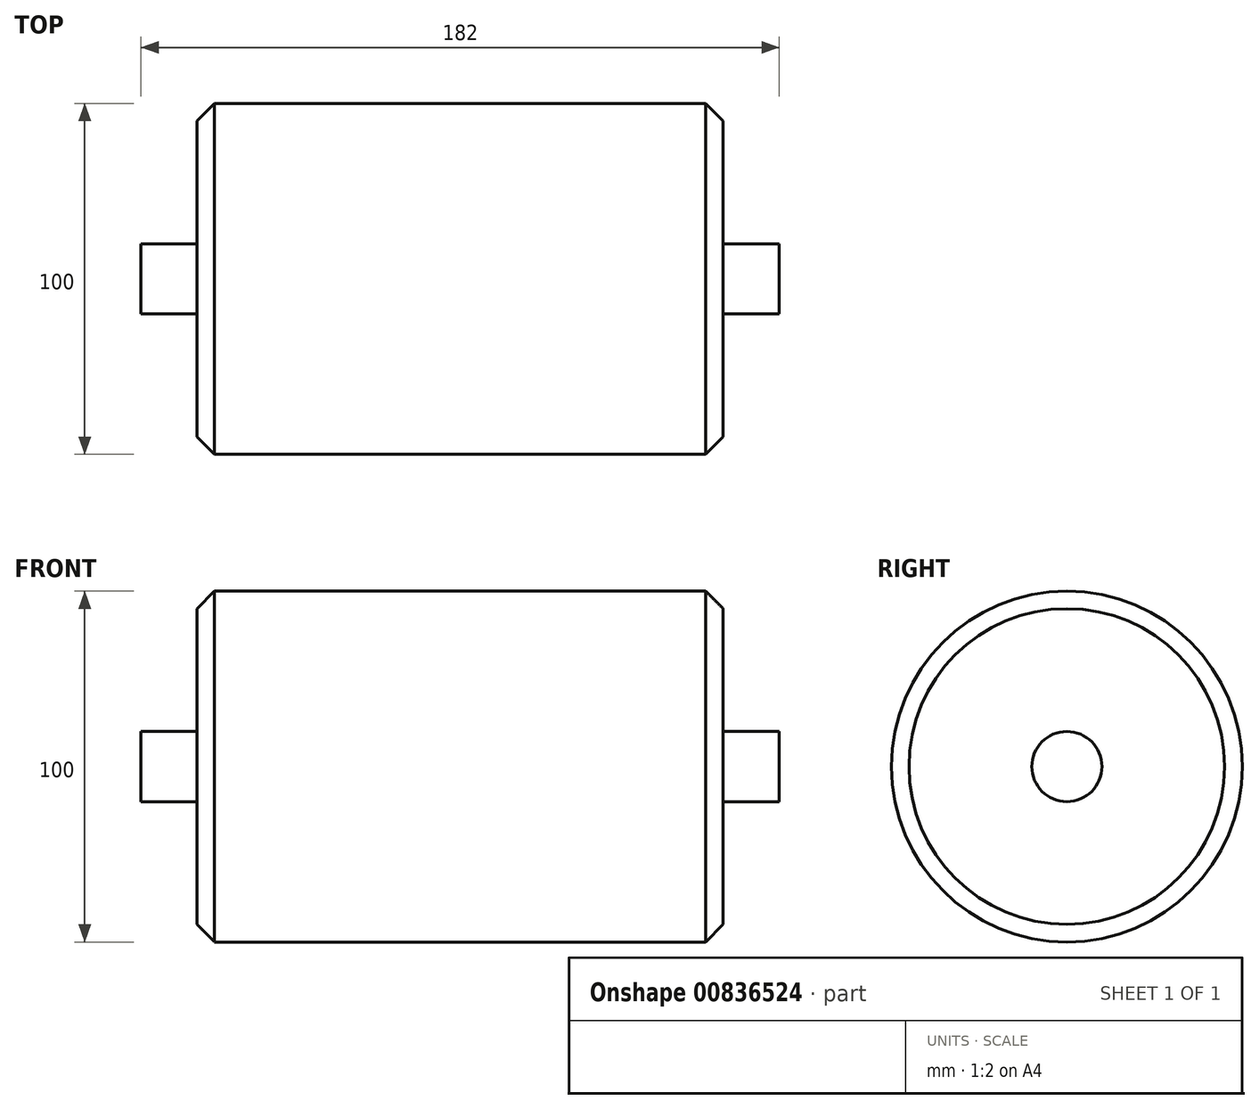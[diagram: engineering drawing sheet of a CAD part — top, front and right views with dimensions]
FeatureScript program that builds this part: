
annotation { "Feature Type Name" : "Feature", "Feature Type Description" : "" }
export const myFeature = defineFeature(function(context is Context, id is Id, definition is map)
    precondition{}
    {
        {
            var Q0;
            Q0=qCreatedBy(makeId("Top.planeOp"),FACE);
            var sketch = newSketch(context, id + "F0", { "sketchPlane" : qUnion([Q0])});
            skLineSegment(sketch, "E0", {"start": v(-91, 0) * mm, "end": v(-91, 10) * mm});
            skLineSegment(sketch, "E1", {"start": v(-91, 10) * mm, "end": v(-75, 10) * mm});
            skLineSegment(sketch, "E2", {"start": v(-75, 10) * mm, "end": v(-75, 50) * mm});
            skLineSegment(sketch, "E3", {"start": v(-75, 50) * mm, "end": v(75, 50) * mm});
            skLineSegment(sketch, "E4", {"start": v(75, 50) * mm, "end": v(75, 10) * mm});
            skLineSegment(sketch, "E5", {"start": v(75, 10) * mm, "end": v(91, 10) * mm});
            skLineSegment(sketch, "E6", {"start": v(91, 10) * mm, "end": v(91, 0) * mm});
            skLineSegment(sketch, "E7", {"start": v(91, 0) * mm, "end": v(-91, 0) * mm});
            skSolve(sketch);
        }
        {
            var Q0;
            Q0=makeQuery(id+"F0.imprint","IMPRINT",FACE,{"disambiguationData":[TD([[makeQuery(id+"F0.imprint","IMPRINT",EDGE,{"derivedFrom":sQuery(id+"F0.wireOp",EDGE,"E0")}),-1.0]])]});
            var Q1;
            Q1=sQuery(id+"F0.wireOp",EDGE,"E7");
            revolve(context, id + "F1", {"surfaceOperationType" : NewSurfaceOperationType.NEW, "entities" : qUnion([Q0]), "axis" : qUnion([Q1]), "revolveType" : RevolveType.FULL});
        }
        {
            var Q0;
            Q0=makeQuery(id+"F1.opRevolve","SWEPT_EDGE",EDGE,{"disambiguationData":[OSD([sQuery(id+"F0.wireOp",EDGE,"E2"),sQuery(id+"F0.wireOp",EDGE,"E3")])]});
            var Q1;
            Q1=makeQuery(id+"F1.opRevolve","SWEPT_EDGE",EDGE,{"disambiguationData":[OSD([sQuery(id+"F0.wireOp",EDGE,"E3"),sQuery(id+"F0.wireOp",EDGE,"E4")])]});
            chamfer(context, id + "F2", {"entities" : qUnion([Q0, Q1]), "width" : 5 * mm, "tangentPropagation" : true});
        }
    });
